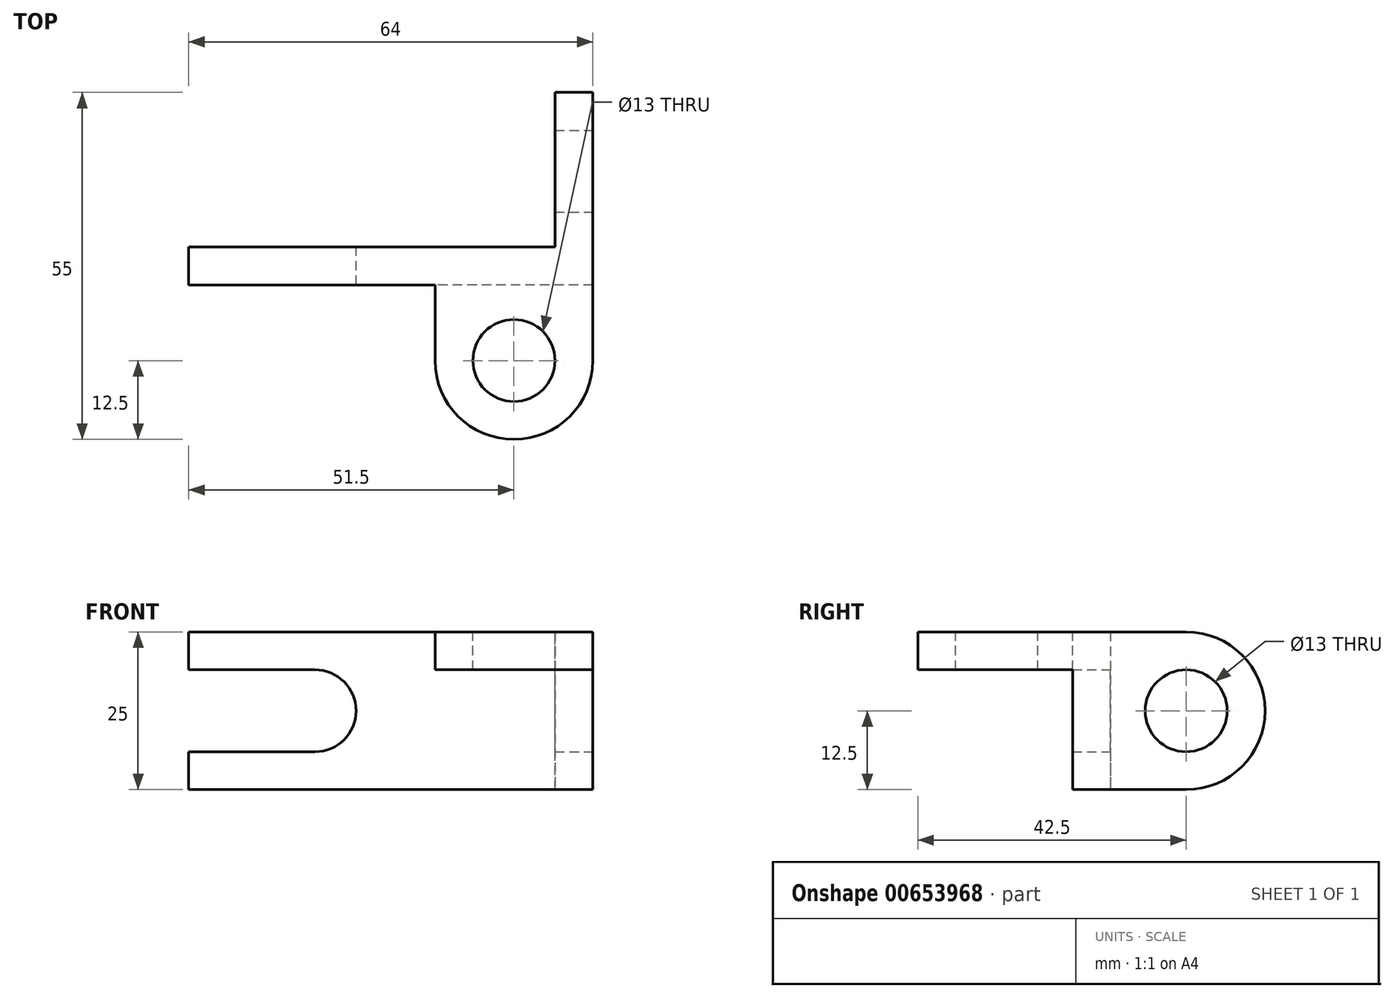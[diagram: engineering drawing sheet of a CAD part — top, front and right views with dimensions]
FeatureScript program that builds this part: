
annotation { "Feature Type Name" : "Feature", "Feature Type Description" : "" }
export const myFeature = defineFeature(function(context is Context, id is Id, definition is map)
    precondition{}
    {
        {
            var Q0;
            Q0=qCreatedBy(makeId("Front.planeOp"),FACE);
            var sketch = newSketch(context, id + "F0", { "sketchPlane" : qUnion([Q0])});
            skLineSegment(sketch, "E0.bottom", {"start": v(32, 12.5) * mm, "end": v(-32, 12.5) * mm});
            skLineSegment(sketch, "E0.top", {"start": v(32, -12.5) * mm, "end": v(-32, -12.5) * mm});
            skLineSegment(sketch, "E0.left", {"start": v(32, 12.5) * mm, "end": v(32, -12.5) * mm});
            skLineSegment(sketch, "E0.right", {"start": v(-32, 12.5) * mm, "end": v(-32, -12.5) * mm});
            skPoint(sketch, "E0.middle", {"position": v(0, 0) * mm});
            skLineSegment(sketch, "E1.bottom", {"start": v(12.5, -12.5) * mm, "end": v(-12.5, -12.5) * mm});
            skLineSegment(sketch, "E1.top", {"start": v(12.5, -12.5) * mm, "end": v(-12.5, -12.5) * mm});
            skLineSegment(sketch, "E1.left", {"start": v(12.5, -12.5) * mm, "end": v(12.5, -12.5) * mm});
            skLineSegment(sketch, "E1.right", {"start": v(-12.5, -12.5) * mm, "end": v(-12.5, -12.5) * mm});
            skPoint(sketch, "E1.middle", {"position": v(0, -12.5) * mm});
            skLineSegment(sketch, "E2", {"start": v(-32, 32.21) * mm, "end": v(-32, -36.66) * mm});
            skLineSegment(sketch, "E3.bottom", {"start": v(-32, 6.5) * mm, "end": v(-12, 6.5) * mm});
            skLineSegment(sketch, "E3.top", {"start": v(-32, -6.5) * mm, "end": v(-12, -6.5) * mm});
            skLineSegment(sketch, "E3.left", {"start": v(-32, 6.5) * mm, "end": v(-32, -6.5) * mm});
            skLineSegment(sketch, "E3.right", {"start": v(-12, 6.5) * mm, "end": v(-12, -6.5) * mm});
            skPoint(sketch, "E3.middle", {"position": v(-22, 0) * mm});
            skCircle(sketch, "E4", {"center": v(-12, 0) * mm, "radius": 6.5 * mm});
            skSolve(sketch);
        }
        {
            var Q0;
            {var subQ9=sQuery(id+"F0.wireOp",EDGE,"E0.bottom");Q0=makeQuery(id+"F0.imprint","IMPRINT",FACE,{"disambiguationData":[TD([[makeQuery(id+"F0.imprint","IMPRINT",EDGE,{"derivedFrom":subQ9}),1.0]])]});}
            extrude(context, id + "F1", {"entities" : qUnion([Q0]), "depth" : 6 * mm, "offsetDistance" : 25 * mm});
        }
        {
            var Q0;
            Q0=makeQuery(id+"F1.opExtrude","SWEPT_FACE",FACE,{"disambiguationData":[OSD([sQuery(id+"F0.wireOp",EDGE,"E0.left")])]});
            var sketch = newSketch(context, id + "F2", { "sketchPlane" : qUnion([Q0])});
            skLineSegment(sketch, "E5.bottom", {"start": v(-6, -12.5) * mm, "end": v(12, -12.5) * mm});
            skLineSegment(sketch, "E5.top", {"start": v(-6, 12.5) * mm, "end": v(12, 12.5) * mm});
            skLineSegment(sketch, "E5.left", {"start": v(-6, -12.5) * mm, "end": v(-6, 12.5) * mm});
            skArc(sketch, "E6", {"start": v(12, -12.5) * mm, "mid": v(24.5, 0) * mm, "end": v(12, 12.5) * mm});
            skCircle(sketch, "E7", {"center": v(12, 0) * mm, "radius": 6.5 * mm});
            skSolve(sketch);
        }
        {
            var Q0;
            {var subQ2=sQuery(id+"F2.wireOp",EDGE,"E6");Q0=makeQuery(id+"F2.imprint","IMPRINT",FACE,{"disambiguationData":[TD([[makeQuery(id+"F2.imprint","IMPRINT",EDGE,{"derivedFrom":subQ2}),1.0]])]});}
            extrude(context, id + "F3", {"entities" : qUnion([Q0]), "operationType" : NewBodyOperationType.ADD, "oppositeDirection" : true, "depth" : 6 * mm, "offsetDistance" : 25 * mm});
        }
        {
            var Q0;
            Q0=makeQuery(id+"F3.boolean.opBoolean","MERGE",FACE,{"derivedFrom":[makeQuery(id+"F1.opExtrude","SWEPT_FACE",FACE,{"disambiguationData":[OSD([sQuery(id+"F0.wireOp",EDGE,"E0.bottom")])]}),makeQuery(id+"F3.opExtrude","SWEPT_FACE",FACE,{"disambiguationData":[OSD([sQuery(id+"F2.wireOp",EDGE,"E5.top")])]})]});
            var sketch = newSketch(context, id + "F4", { "sketchPlane" : qUnion([Q0])});
            skLineSegment(sketch, "E8.bottom", {"start": v(32, 0) * mm, "end": v(7, 0) * mm});
            skLineSegment(sketch, "E8.left", {"start": v(32, 0) * mm, "end": v(32, -18) * mm});
            skLineSegment(sketch, "E8.right", {"start": v(7, 0) * mm, "end": v(7, -18) * mm});
            skArc(sketch, "E9", {"start": v(7, -18) * mm, "mid": v(19.5, -30.5) * mm, "end": v(32, -18) * mm});
            skCircle(sketch, "E10", {"center": v(19.5, -18) * mm, "radius": 6.5 * mm});
            skSolve(sketch);
        }
        {
            var Q0;
            {var subQ0=sQuery(id+"F4.wireOp",EDGE,"E9");Q0=makeQuery(id+"F4.imprint","IMPRINT",FACE,{"disambiguationData":[TD([[makeQuery(id+"F4.imprint","IMPRINT",EDGE,{"derivedFrom":subQ0}),1.0]])]});}
            extrude(context, id + "F5", {"entities" : qUnion([Q0]), "operationType" : NewBodyOperationType.ADD, "oppositeDirection" : true, "depth" : 6 * mm, "offsetDistance" : 25 * mm});
        }
    });
